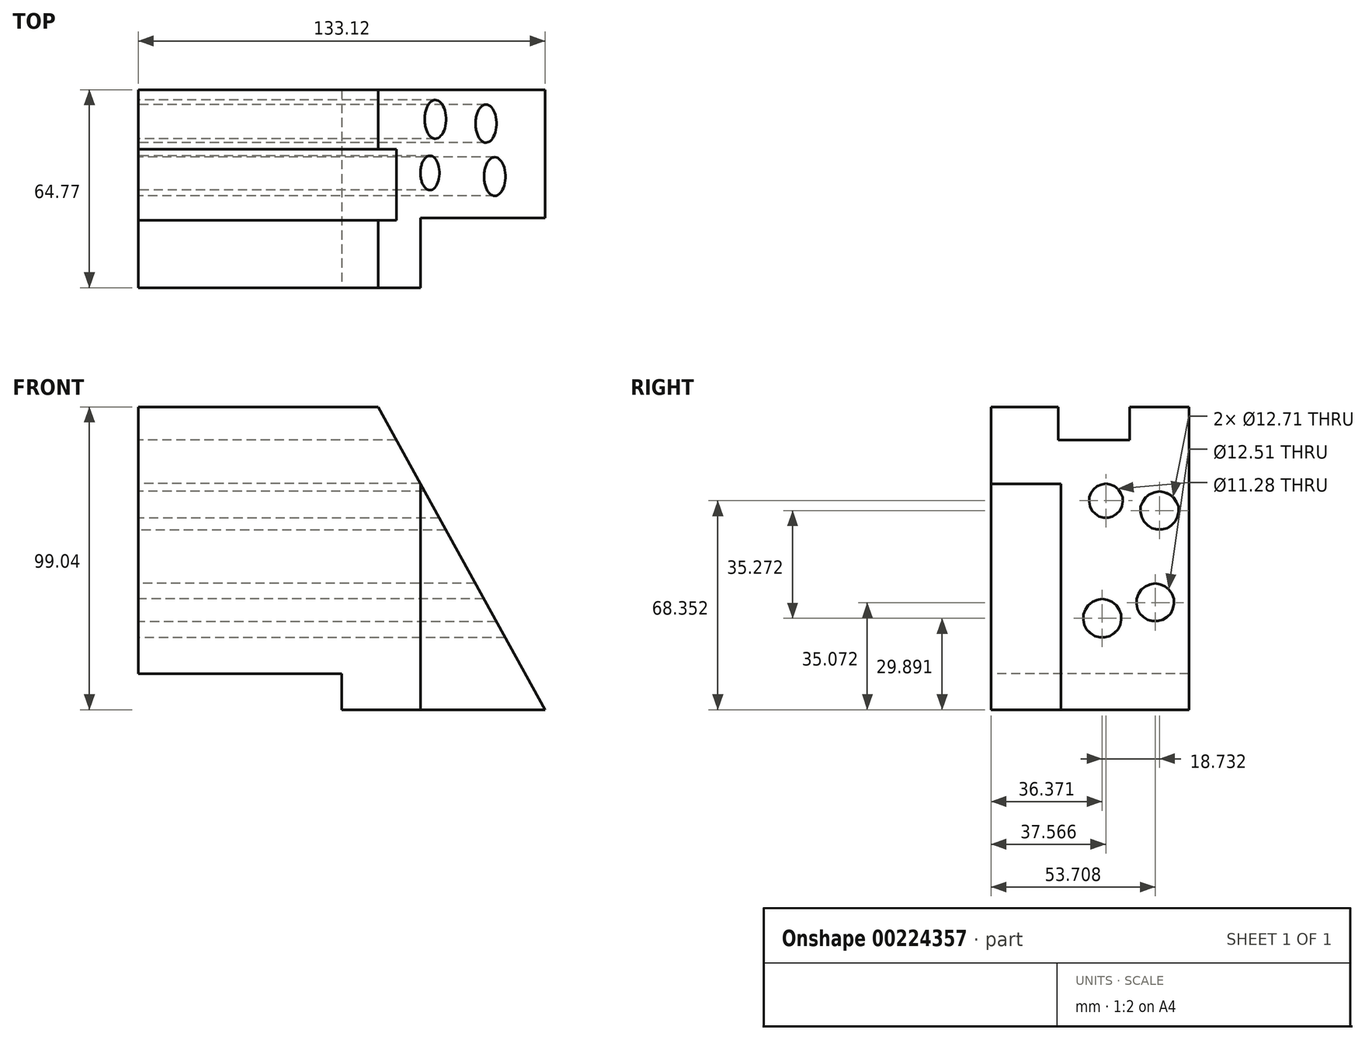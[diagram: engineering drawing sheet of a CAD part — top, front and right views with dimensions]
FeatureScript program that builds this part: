
annotation { "Feature Type Name" : "Feature", "Feature Type Description" : "" }
export const myFeature = defineFeature(function(context is Context, id is Id, definition is map)
    precondition{}
    {
        {
            var Q0;
            Q0=qCreatedBy(makeId("Front.planeOp"),FACE);
            var sketch = newSketch(context, id + "F0", { "sketchPlane" : qUnion([Q0])});
            skLineSegment(sketch, "E0.bottom", {"start": v(11.96, 49.52) * mm, "end": v(-66.56, 49.52) * mm});
            skLineSegment(sketch, "E0.top", {"start": v(66.56, -49.52) * mm, "end": v(-66.56, -49.52) * mm});
            skLineSegment(sketch, "E0.right", {"start": v(-66.56, 49.52) * mm, "end": v(-66.56, -49.52) * mm});
            skPoint(sketch, "E0.middle", {"position": v(0, 0) * mm});
            skLineSegment(sketch, "E1", {"start": v(11.96, 49.52) * mm, "end": v(66.56, -49.52) * mm});
            skPoint(sketch, "E0.left.start.orphan", {"position": v(66.56, 49.52) * mm});
            skSolve(sketch);
        }
        {
            var Q0;
            Q0 = qSketchRegion(id + "F0", true);
            extrude(context, id + "F1", {"entities" : qUnion([Q0]), "depth" : 33.78 * mm, "hasSecondDirection" : true, "secondDirectionOppositeDirection" : true, "secondDirectionDepth" : 30.99 * mm});
        }
        {
            var Q0;
            Q0=makeQuery(id+"F1.opExtrude","SWEPT_FACE",FACE,{"disambiguationData":[OSD([sQuery(id+"F0.wireOp",EDGE,"E0.right")])]});
            var sketch = newSketch(context, id + "F2", { "sketchPlane" : qUnion([Q0])});
            skLineSegment(sketch, "E2.bottom", {"start": v(-11.56, 49.52) * mm, "end": v(11.76, 49.52) * mm});
            skLineSegment(sketch, "E2.top", {"start": v(-11.56, 38.76) * mm, "end": v(11.76, 38.76) * mm});
            skLineSegment(sketch, "E2.left", {"start": v(-11.56, 49.52) * mm, "end": v(-11.56, 38.76) * mm});
            skLineSegment(sketch, "E2.right", {"start": v(11.76, 49.52) * mm, "end": v(11.76, 38.76) * mm});
            skSolve(sketch);
        }
        {
            var Q0;
            Q0 = qSketchRegion(id + "F2", true);
            extrude(context, id + "F3", {"entities" : qUnion([Q0]), "operationType" : NewBodyOperationType.REMOVE, "oppositeDirection" : true, "depth" : 133.35 * mm});
        }
        {
            var Q0;
            Q0=makeQuery(id+"F1.opExtrude","SWEPT_FACE",FACE,{"disambiguationData":[OSD([sQuery(id+"F0.wireOp",EDGE,"E0.top")])]});
            var sketch = newSketch(context, id + "F4", { "sketchPlane" : qUnion([Q0])});
            skLineSegment(sketch, "E3.bottom", {"start": v(66.56, 33.78) * mm, "end": v(25.8, 33.78) * mm});
            skLineSegment(sketch, "E3.top", {"start": v(66.56, 10.96) * mm, "end": v(25.8, 10.96) * mm});
            skLineSegment(sketch, "E3.left", {"start": v(66.56, 33.78) * mm, "end": v(66.56, 10.96) * mm});
            skLineSegment(sketch, "E3.right", {"start": v(25.8, 33.78) * mm, "end": v(25.8, 10.96) * mm});
            skSolve(sketch);
        }
        {
            var Q0;
            Q0 = qSketchRegion(id + "F4", true);
            extrude(context, id + "F5", {"entities" : qUnion([Q0]), "operationType" : NewBodyOperationType.REMOVE, "oppositeDirection" : true, "depth" : 113.8 * mm});
        }
        {
            var Q0;
            Q0=makeQuery(id+"F1.opExtrude","SWEPT_FACE",FACE,{"disambiguationData":[OSD([sQuery(id+"F0.wireOp",EDGE,"E0.right")])]});
            var sketch = newSketch(context, id + "F6", { "sketchPlane" : qUnion([Q0])});
            skCircle(sketch, "E4", {"center": v(-21.32, 15.64) * mm, "radius": 6.36 * mm});
            skCircle(sketch, "E5", {"center": v(-3.79, 18.83) * mm, "radius": 5.64 * mm});
            skCircle(sketch, "E6", {"center": v(-19.93, -14.45) * mm, "radius": 6.25 * mm});
            skCircle(sketch, "E7", {"center": v(-2.6, -19.63) * mm, "radius": 6.36 * mm});
            skSolve(sketch);
        }
        {
            var Q0;
            Q0 = qSketchRegion(id + "F6", true);
            extrude(context, id + "F7", {"entities" : qUnion([Q0]), "operationType" : NewBodyOperationType.REMOVE, "oppositeDirection" : true, "depth" : 204.98 * mm});
        }
        {
            var Q0;
            Q0=makeQuery(id+"F1.opExtrude","CAP_FACE",FACE,{"disambiguationData":[OSD([sQuery(id+"F0.wireOp",EDGE,"E0.bottom"),sQuery(id+"F0.wireOp",EDGE,"E0.top"),sQuery(id+"F0.wireOp",EDGE,"E0.right"),sQuery(id+"F0.wireOp",EDGE,"E1")])],"isStart":false});
            var sketch = newSketch(context, id + "F8", { "sketchPlane" : qUnion([Q0])});
            skLineSegment(sketch, "E8.bottom", {"start": v(-66.56, -49.52) * mm, "end": v(0, -49.52) * mm});
            skLineSegment(sketch, "E8.top", {"start": v(-66.56, -37.76) * mm, "end": v(0, -37.76) * mm});
            skLineSegment(sketch, "E8.left", {"start": v(-66.56, -49.52) * mm, "end": v(-66.56, -37.76) * mm});
            skLineSegment(sketch, "E8.right", {"start": v(0, -49.52) * mm, "end": v(0, -37.76) * mm});
            skSolve(sketch);
        }
        {
            var Q0;
            Q0 = qSketchRegion(id + "F8", true);
            extrude(context, id + "F9", {"entities" : qUnion([Q0]), "operationType" : NewBodyOperationType.REMOVE, "oppositeDirection" : true, "depth" : 176.53 * mm});
        }
    });
